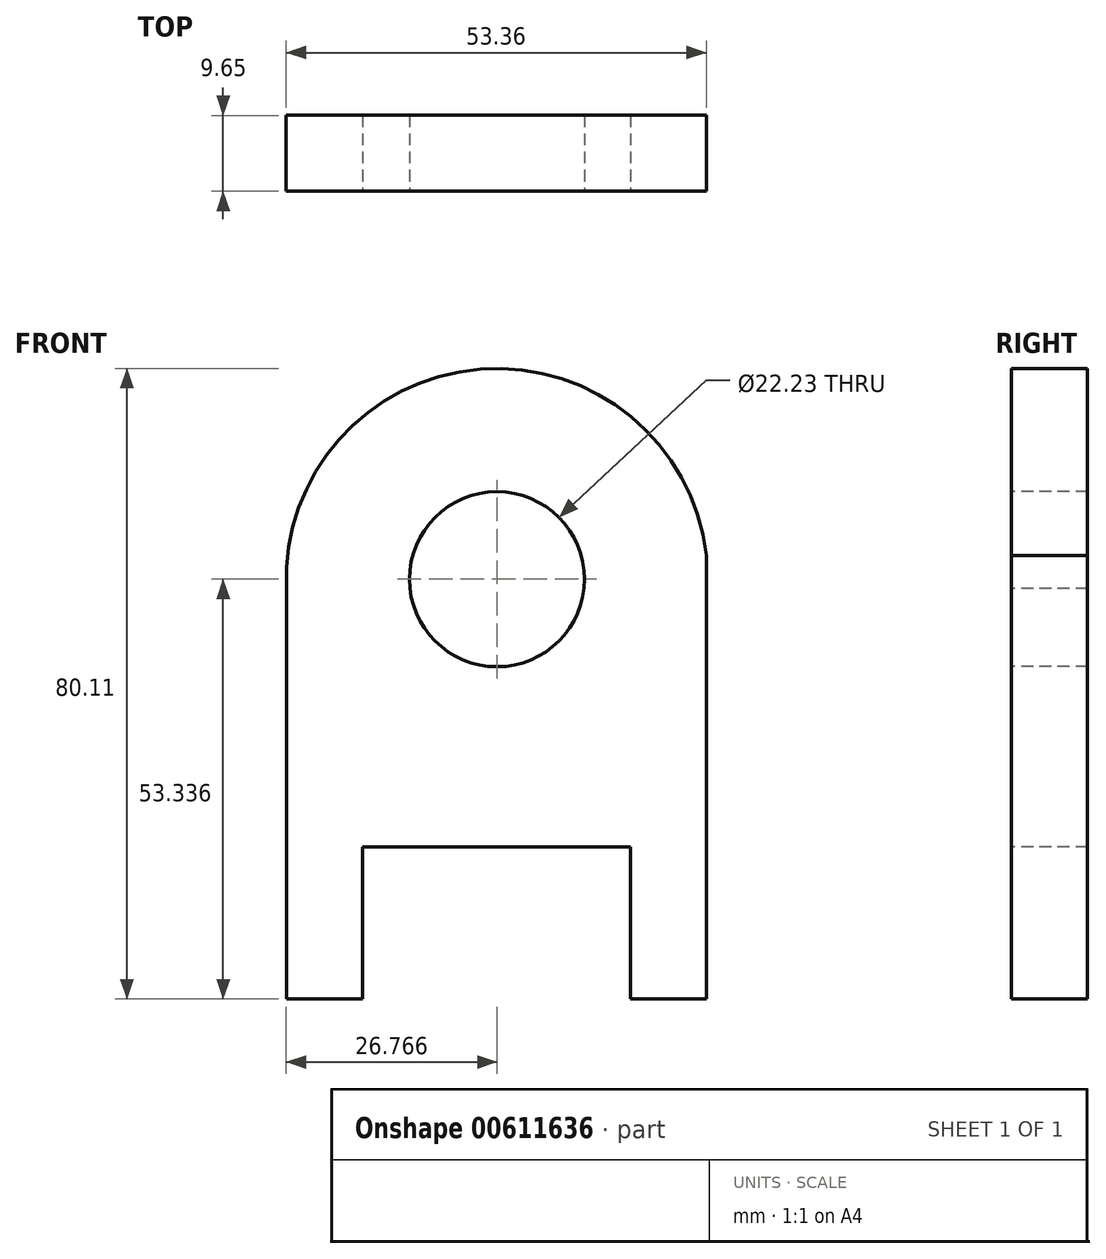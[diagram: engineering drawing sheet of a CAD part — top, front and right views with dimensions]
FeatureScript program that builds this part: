
annotation { "Feature Type Name" : "Feature", "Feature Type Description" : "" }
export const myFeature = defineFeature(function(context is Context, id is Id, definition is map)
    precondition{}
    {
        {
            var Q0;
            Q0=qCreatedBy(makeId("Front.planeOp"),FACE);
            var sketch = newSketch(context, id + "F0", { "sketchPlane" : qUnion([Q0])});
            skLineSegment(sketch, "E0", {"start": v(-34.04, 0) * mm, "end": v(0, 0) * mm});
            skLineSegment(sketch, "E1", {"start": v(-34.04, -19.3) * mm, "end": v(-34.04, 0) * mm});
            skLineSegment(sketch, "E2", {"start": v(-34.04, -19.3) * mm, "end": v(-87.38, -19.3) * mm});
            skLineSegment(sketch, "E3", {"start": v(-87.38, -19.3) * mm, "end": v(-87.38, 0) * mm});
            skLineSegment(sketch, "E4", {"start": v(0, 0) * mm, "end": v(-87.38, 0) * mm});
            skPoint(sketch, "E5", {"position": v(-43.69, 0) * mm});
            skLineSegment(sketch, "E6", {"start": v(0, 0) * mm, "end": v(0, -19.3) * mm});
            skLineSegment(sketch, "E7", {"start": v(-43.69, 0) * mm, "end": v(-43.69, -19.3) * mm});
            skLineSegment(sketch, "E8", {"start": v(-87.38, 0) * mm, "end": v(-87.38, 32.83) * mm});
            skLineSegment(sketch, "E9", {"start": v(-34.04, 0) * mm, "end": v(-34.04, 37.06) * mm});
            skArc(sketch, "E10", {"start": v(-34.04, 37.06) * mm, "mid": v(-62.75, 60.72) * mm, "end": v(-87.38, 32.83) * mm});
            skCircle(sketch, "E11", {"center": v(-60.63, 34.04) * mm, "radius": 11.11 * mm});
            skLineSegment(sketch, "E12", {"start": v(-60.63, 34.04) * mm, "end": v(-34.04, 34.04) * mm});
            skLineSegment(sketch, "E13", {"start": v(-77.72, 0) * mm, "end": v(-77.72, -19.3) * mm});
            skLineSegment(sketch, "E14", {"start": v(-34.04, 0) * mm, "end": v(-43.69, 0) * mm});
            skLineSegment(sketch, "E15", {"start": v(-77.72, 0) * mm, "end": v(-87.38, 0) * mm});
            skSolve(sketch);
        }
        {
            var Q0;
            {var subQ0=sQuery(id+"F0.wireOp",EDGE,"E3");Q0=makeQuery(id+"F0.imprint","IMPRINT",FACE,{"disambiguationData":[TD([[makeQuery(id+"F0.imprint","IMPRINT",EDGE,{"derivedFrom":subQ0}),-1.0]])]});}
            var Q1;
            {var subQ0=sQuery(id+"F0.wireOp",EDGE,"E1");Q1=makeQuery(id+"F0.imprint","IMPRINT",FACE,{"disambiguationData":[TD([[makeQuery(id+"F0.imprint","IMPRINT",EDGE,{"derivedFrom":subQ0}),1.0]])]});}
            var Q2;
            Q2=makeQuery(id+"F0.imprint","IMPRINT",FACE,{"disambiguationData":[TD([[makeQuery(id+"F0.imprint","IMPRINT",EDGE,{"derivedFrom":sQuery(id+"F0.wireOp",EDGE,"E8")}),-1.0]])]});
            extrude(context, id + "F1", {"entities" : qUnion([Q0, Q1, Q2]), "oppositeDirection" : true, "depth" : 9.65 * mm, "offsetDistance" : 25.4 * mm});
        }
    });
